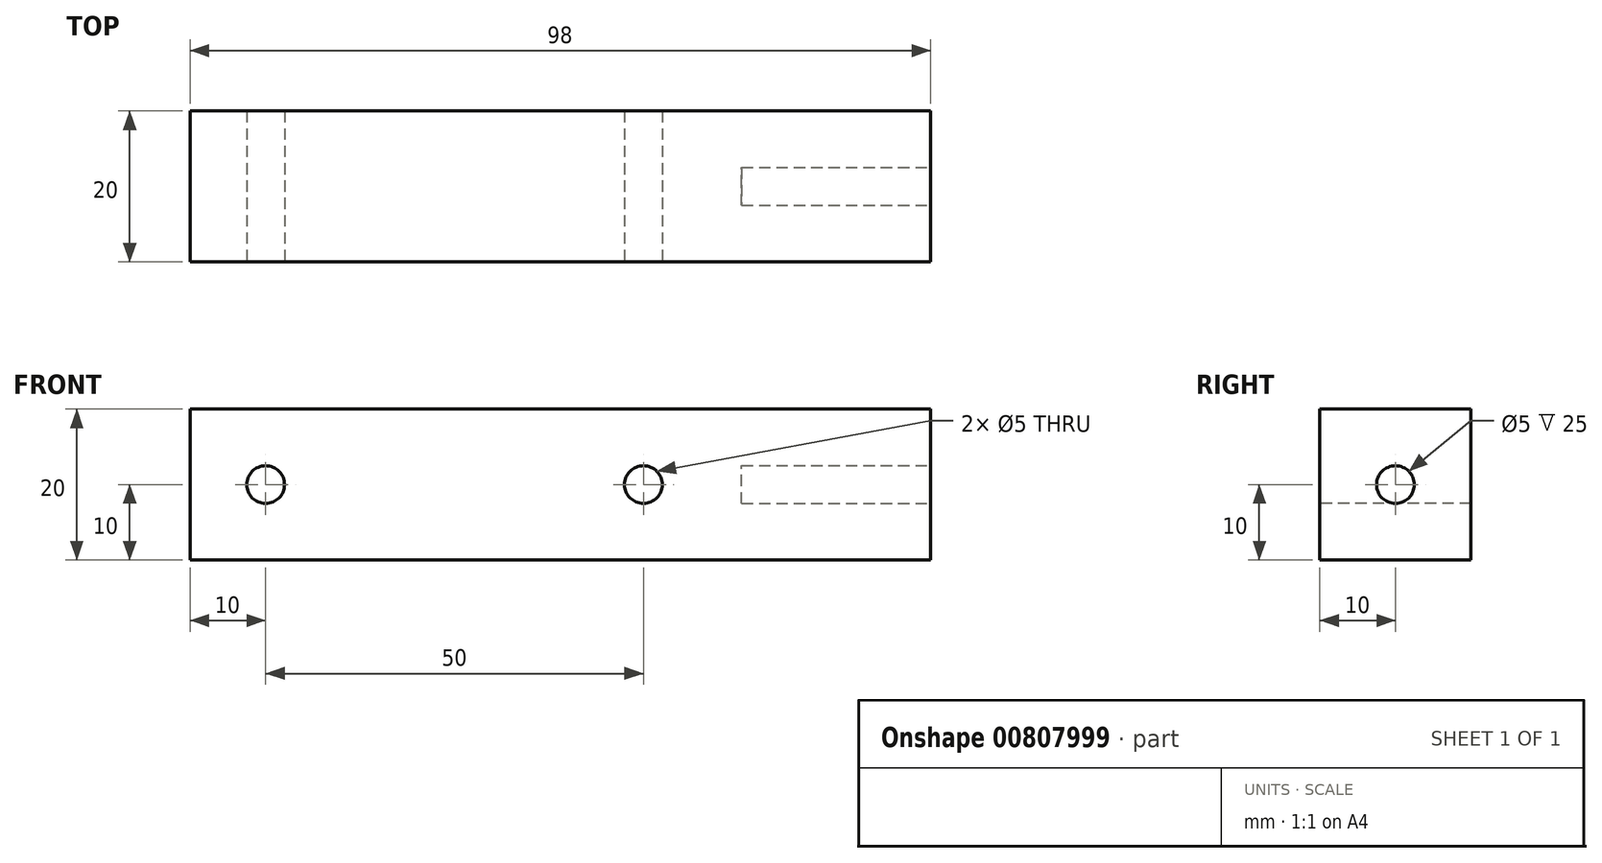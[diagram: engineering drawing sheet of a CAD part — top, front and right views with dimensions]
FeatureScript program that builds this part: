
annotation { "Feature Type Name" : "Feature", "Feature Type Description" : "" }
export const myFeature = defineFeature(function(context is Context, id is Id, definition is map)
    precondition{}
    {
        {
            var Q0;
            Q0=qCreatedBy(makeId("Front.planeOp"),FACE);
            var sketch = newSketch(context, id + "F0", { "sketchPlane" : qUnion([Q0])});
            skLineSegment(sketch, "E0.bottom", {"start": v(0, 0) * mm, "end": v(98, 0) * mm});
            skLineSegment(sketch, "E0.top", {"start": v(0, 20) * mm, "end": v(98, 20) * mm});
            skLineSegment(sketch, "E0.left", {"start": v(0, 0) * mm, "end": v(0, 20) * mm});
            skLineSegment(sketch, "E0.right", {"start": v(98, 0) * mm, "end": v(98, 20) * mm});
            skSolve(sketch);
        }
        {
            var Q0;
            Q0 = qSketchRegion(id + "F0", true);
            extrude(context, id + "F1", {"entities" : qUnion([Q0]), "depth" : 20 * mm, "offsetDistance" : 25 * mm});
        }
        {
            var Q0;
            Q0=makeQuery(id+"F1.opExtrude","SWEPT_FACE",FACE,{"disambiguationData":[OSD([sQuery(id+"F0.wireOp",EDGE,"E0.right")])]});
            var sketch = newSketch(context, id + "F2", { "sketchPlane" : qUnion([Q0])});
            skCircle(sketch, "E1", {"center": v(-10, 10) * mm, "radius": 2.5 * mm});
            skPoint(sketch, "E1.centerSnap0", {"position": v(-10, 20) * mm});
            skPoint(sketch, "E1.centerSnap1", {"position": v(-20, 10) * mm});
            skSolve(sketch);
        }
        {
            var Q0;
            Q0=makeQuery(id+"F2.imprint","IMPRINT",FACE,{"disambiguationData":[TD([[makeQuery(id+"F2.imprint","IMPRINT",EDGE,{"derivedFrom":sQuery(id+"F2.wireOp",EDGE,"E1")}),1.0]])]});
            extrude(context, id + "F3", {"entities" : qUnion([Q0]), "operationType" : NewBodyOperationType.REMOVE, "oppositeDirection" : true, "depth" : 25 * mm, "offsetDistance" : 25 * mm});
        }
        {
            var Q0;
            Q0=makeQuery(id+"F1.opExtrude","CAP_FACE",FACE,{"disambiguationData":[OSD([sQuery(id+"F0.wireOp",EDGE,"E0.bottom"),sQuery(id+"F0.wireOp",EDGE,"E0.top"),sQuery(id+"F0.wireOp",EDGE,"E0.left"),sQuery(id+"F0.wireOp",EDGE,"E0.right")])],"isStart":false});
            var sketch = newSketch(context, id + "F4", { "sketchPlane" : qUnion([Q0])});
            skCircle(sketch, "E2", {"center": v(10, 10) * mm, "radius": 2.5 * mm});
            skPoint(sketch, "E2.centerSnap0", {"position": v(0, 10) * mm});
            skCircle(sketch, "E3", {"center": v(60, 10) * mm, "radius": 2.5 * mm});
            skSolve(sketch);
        }
        {
            var Q0;
            Q0 = qSketchRegion(id + "F4", true);
            extrude(context, id + "F5", {"entities" : qUnion([Q0]), "operationType" : NewBodyOperationType.REMOVE, "endBound" : BoundingType.THROUGH_ALL, "oppositeDirection" : true, "depth" : 25 * mm, "offsetDistance" : 25 * mm});
        }
    });
